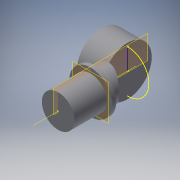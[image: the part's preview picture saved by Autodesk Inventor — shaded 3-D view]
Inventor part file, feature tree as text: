
AUTODESK INVENTOR PART (.ipt)
format: ipt  version: 2018 (Build 220112000, 112)  size: 133,120 bytes
history: native  units: in
note: dims shown in document units (in); Inventor stores cm internally (conversion verified against a paired STEP export)
features: extrude x4, other x4, sketch x4, plane x2
ambient origin geometry x8: Origin, YZ Plane, XZ Plane, XY Plane, X Axis, Y Axis, Z Axis, Center Point
bodies: Solid1 (feature_tree)
feature tree (14):
  extrude  "Extrusion1"  Depth=1.315in
  plane  "Work Plane1"
  extrude  "Extrusion2"  [1 undecoded]
  other  "Work Axis1"
  sketch  "Sketch4"  dims[d6=1.315in d7=0.125in d8=0.0in]
  other  "Work Point2"
  plane  "Work Plane2"
  sketch  "Sketch5"  dims[d9=1.5in d10=0.5in d11=0.0in d12=0.8in d13=0.0in]
  extrude  "Extrusion3"  Depth=0.125in TaperAngle=0.0deg
  extrude  "Extrusion4"  Depth=0.8in TaperAngle=0.0deg
  sketch  "Sketch1"  dims[d0=1.0in d1=1.315in]
  sketch  "Sketch3"  dims[d2=2.125in d3=0.0in d5=-1.0in]
  other  "Work Point1"
  other  "Work Point3"
note: 1 required parameter value undecoded (feature->parameter linkage not recoverable at this tier; creation-order binding heuristic only, values carry confidence <= 0.55)
